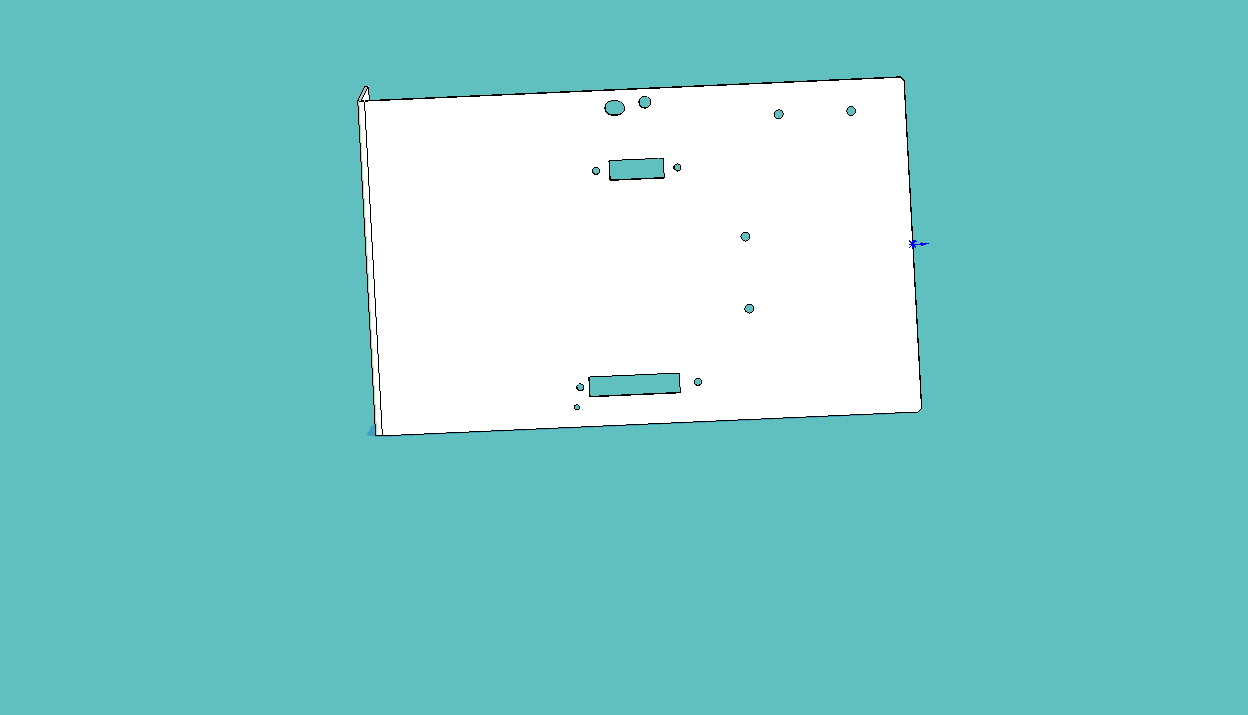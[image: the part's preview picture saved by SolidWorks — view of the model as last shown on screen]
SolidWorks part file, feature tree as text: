
SOLIDWORKS PART (.sldprt)
format: sldprt  version: not decoded by parser v0  size: 384,000 bytes
history: native  units: mm
features: chamfer x4, plane x3, sketch x3, cut_extrude x2, fillet x2, material x1, extrude x1 (+10 scaffold rows collapsed)
feature tree (26):
  scaffold x10  (default folders/planes/origin — collapsed)
  material  "Matériau <non spécifié>"
  plane  "Plan de face"
  plane  "Plan de dessus"
  plane  "Plan de droite"
  sketch  "Esquisse1"  dims[D1=2.0mm D2=300.0mm D3=63.0mm]
  extrude  "Extrusion1"  Depth=186mm
  sketch  "Esquisse2"  dims[c1.D5=4.0mm c1.D13=~9.20708mm c1.D16=6.7mm c1.D17=4.0mm c1.D20=5.0mm c1.D21=5.0mm c1.D26=5.0mm c1.D27=3.0mm c1.D28=3.0mm c1.D29=3.0mm c1.D1=22.0mm c1.D2=11.0mm c1.D3=50.0mm c1.D4=65.0mm c1.D6=10.0mm c1.D7=122.5mm c1.D8=127.5mm c1.D9=30.0mm c1.D10=11.0mm c1.D11=45.0mm c1.D12=119.5mm c2.D13=143.5mm c2.D14=158.75mm c2.D15=7.5mm c2.D18=3.0mm c2.D19=10.0mm c2.D21=30.0mm c2.D22=40.0mm c2.D23=92.0mm c2.D24=40.0mm c2.D25=27.5mm c2.D26=61.5mm c3.D25=17.5mm c3.D28=11.0mm c3.D29=190.0mm]
  cut_extrude  "Enlèv. mat.-Extru.1"  [1 undecoded]
  sketch  "Esquisse3"  dims[c1.D1=8.0mm c1.D2=20.0mm c1.D3=158.0mm c2.D1=8.0mm c2.D3=158.0mm c3.D1=150.0mm c3.D3=8.0mm]
  cut_extrude  "Enlèv. mat.-Extru.2"  Depth=20mm
  chamfer  "Chanfrein1"  Distance=5mm Angle=45deg
  fillet  "Congé1"  Radius=2mm
  fillet  "Congé2"  Radius=4mm
  chamfer  "Chanfrein2"  Distance=2mm Angle=45deg
  chamfer  "Chanfrein3"  Distance=2mm Angle=45deg
  chamfer  "Chanfrein4"  Distance=1.5mm Angle=45deg
decode coverage: 11 of 12 modeling features carry decoded parameters
note: ~ marks probable driven/reference dimensions
note: 1 parameter value undecoded
note: suppression state not decoded; provenance and decode notes live in map.json
